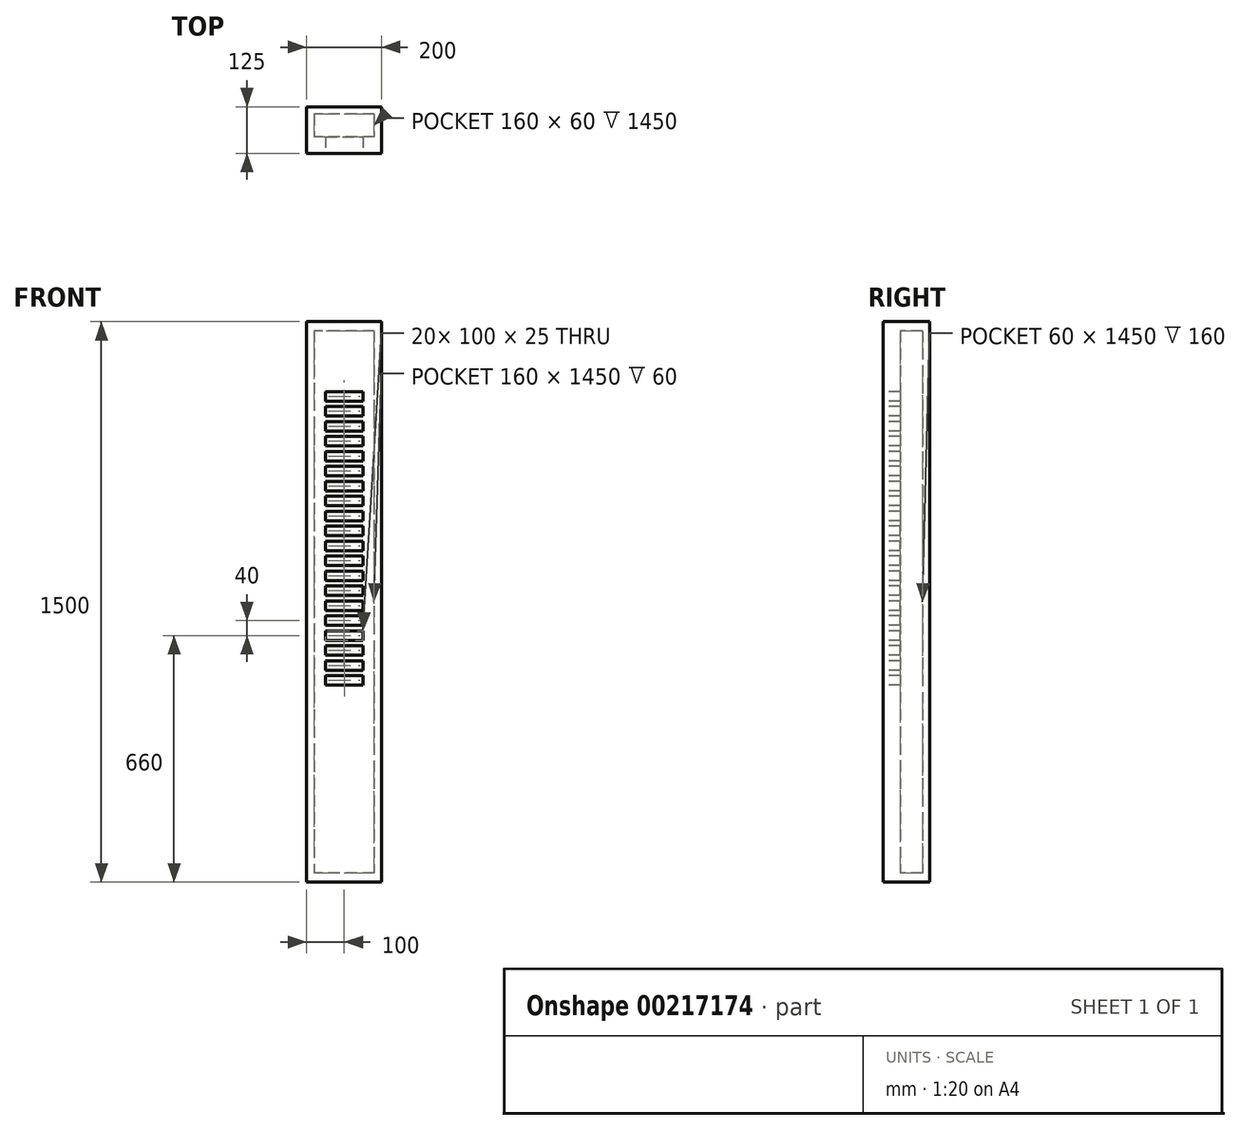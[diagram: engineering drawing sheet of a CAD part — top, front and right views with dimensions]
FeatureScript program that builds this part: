
annotation { "Feature Type Name" : "Feature", "Feature Type Description" : "" }
export const myFeature = defineFeature(function(context is Context, id is Id, definition is map)
    precondition{}
    {
        {
            var Q0;
            Q0=qCreatedBy(makeId("Front.planeOp"),FACE);
            var sketch = newSketch(context, id + "F0", { "sketchPlane" : qUnion([Q0])});
            skLineSegment(sketch, "E0.bottom", {"start": v(-100, 750) * mm, "end": v(100, 750) * mm});
            skLineSegment(sketch, "E0.top", {"start": v(-100, -750) * mm, "end": v(100, -750) * mm});
            skLineSegment(sketch, "E0.left", {"start": v(-100, 750) * mm, "end": v(-100, -750) * mm});
            skLineSegment(sketch, "E0.right", {"start": v(100, 750) * mm, "end": v(100, -750) * mm});
            skLineSegment(sketch, "E1.bottom", {"start": v(-50, 562.5) * mm, "end": v(50, 562.5) * mm});
            skLineSegment(sketch, "E1.top", {"start": v(-50, 537.5) * mm, "end": v(50, 537.5) * mm});
            skLineSegment(sketch, "E1.left", {"start": v(-50, 562.5) * mm, "end": v(-50, 537.5) * mm});
            skLineSegment(sketch, "E1.right", {"start": v(50, 562.5) * mm, "end": v(50, 537.5) * mm});
            skPoint(sketch, "E1.middle", {"position": v(0, 550) * mm});
            skLineSegment(sketch, "E2.bottom", {"start": v(-50, 522.5) * mm, "end": v(50, 522.5) * mm});
            skLineSegment(sketch, "E2.top", {"start": v(-50, 497.5) * mm, "end": v(50, 497.5) * mm});
            skLineSegment(sketch, "E2.left", {"start": v(-50, 522.5) * mm, "end": v(-50, 497.5) * mm});
            skLineSegment(sketch, "E2.right", {"start": v(50, 522.5) * mm, "end": v(50, 497.5) * mm});
            skPoint(sketch, "E2.middle", {"position": v(0, 510) * mm});
            skPoint(sketch, "E2.cornerSnap0", {"position": v(-50, 550) * mm});
            skLineSegment(sketch, "E3.bottom", {"start": v(-50, 482.5) * mm, "end": v(50, 482.5) * mm});
            skLineSegment(sketch, "E3.top", {"start": v(-50, 457.5) * mm, "end": v(50, 457.5) * mm});
            skLineSegment(sketch, "E3.left", {"start": v(-50, 482.5) * mm, "end": v(-50, 457.5) * mm});
            skLineSegment(sketch, "E3.right", {"start": v(50, 482.5) * mm, "end": v(50, 457.5) * mm});
            skPoint(sketch, "E3.middle", {"position": v(0, 470) * mm});
            skLineSegment(sketch, "E4.bottom", {"start": v(-50, 442.5) * mm, "end": v(50, 442.5) * mm});
            skLineSegment(sketch, "E4.top", {"start": v(-50, 417.5) * mm, "end": v(50, 417.5) * mm});
            skLineSegment(sketch, "E4.left", {"start": v(-50, 442.5) * mm, "end": v(-50, 417.5) * mm});
            skLineSegment(sketch, "E4.right", {"start": v(50, 442.5) * mm, "end": v(50, 417.5) * mm});
            skPoint(sketch, "E4.middle", {"position": v(0, 430) * mm});
            skLineSegment(sketch, "E5.bottom", {"start": v(-50, 402.5) * mm, "end": v(50, 402.5) * mm});
            skLineSegment(sketch, "E5.top", {"start": v(-50, 377.5) * mm, "end": v(50, 377.5) * mm});
            skLineSegment(sketch, "E5.left", {"start": v(-50, 402.5) * mm, "end": v(-50, 377.5) * mm});
            skLineSegment(sketch, "E5.right", {"start": v(50, 402.5) * mm, "end": v(50, 377.5) * mm});
            skPoint(sketch, "E5.middle", {"position": v(0, 390) * mm});
            skLineSegment(sketch, "E6.bottom", {"start": v(-50, 362.5) * mm, "end": v(50, 362.5) * mm});
            skLineSegment(sketch, "E6.top", {"start": v(-50, 337.5) * mm, "end": v(50, 337.5) * mm});
            skLineSegment(sketch, "E6.left", {"start": v(-50, 362.5) * mm, "end": v(-50, 337.5) * mm});
            skLineSegment(sketch, "E6.right", {"start": v(50, 362.5) * mm, "end": v(50, 337.5) * mm});
            skPoint(sketch, "E6.middle", {"position": v(0, 350) * mm});
            skLineSegment(sketch, "E7.bottom", {"start": v(-50, 322.5) * mm, "end": v(50, 322.5) * mm});
            skLineSegment(sketch, "E7.top", {"start": v(-50, 297.5) * mm, "end": v(50, 297.5) * mm});
            skLineSegment(sketch, "E7.left", {"start": v(-50, 322.5) * mm, "end": v(-50, 297.5) * mm});
            skLineSegment(sketch, "E7.right", {"start": v(50, 322.5) * mm, "end": v(50, 297.5) * mm});
            skPoint(sketch, "E7.middle", {"position": v(0, 310) * mm});
            skLineSegment(sketch, "E8.bottom", {"start": v(-50, 282.5) * mm, "end": v(50, 282.5) * mm});
            skLineSegment(sketch, "E8.top", {"start": v(-50, 257.5) * mm, "end": v(50, 257.5) * mm});
            skLineSegment(sketch, "E8.left", {"start": v(-50, 282.5) * mm, "end": v(-50, 257.5) * mm});
            skLineSegment(sketch, "E8.right", {"start": v(50, 282.5) * mm, "end": v(50, 257.5) * mm});
            skPoint(sketch, "E8.middle", {"position": v(0, 270) * mm});
            skLineSegment(sketch, "E9.bottom", {"start": v(-50, 242.5) * mm, "end": v(50, 242.5) * mm});
            skLineSegment(sketch, "E9.top", {"start": v(-50, 217.5) * mm, "end": v(50, 217.5) * mm});
            skLineSegment(sketch, "E9.left", {"start": v(-50, 242.5) * mm, "end": v(-50, 217.5) * mm});
            skLineSegment(sketch, "E9.right", {"start": v(50, 242.5) * mm, "end": v(50, 217.5) * mm});
            skPoint(sketch, "E9.middle", {"position": v(0, 230) * mm});
            skPoint(sketch, "E10", {"position": v(0, 210) * mm});
            skLineSegment(sketch, "E11.MirrorCS", {"start": v(-49.95, -142.5) * mm, "end": v(-49.95, -117.5) * mm});
            skLineSegment(sketch, "E12.MirrorCS", {"start": v(50, 17.5) * mm, "end": v(50, 42.5) * mm});
            skLineSegment(sketch, "E13.MirrorCS", {"start": v(-50, 57.5) * mm, "end": v(-50, 82.5) * mm});
            skLineSegment(sketch, "E14.MirrorCS", {"start": v(-50, -62.5) * mm, "end": v(-50, -37.5) * mm});
            skLineSegment(sketch, "E15.MirrorCS", {"start": v(-50, 177.5) * mm, "end": v(-50, 202.5) * mm});
            skLineSegment(sketch, "E16.MirrorCS", {"start": v(-50, 17.5) * mm, "end": v(-50, 42.5) * mm});
            skLineSegment(sketch, "E17.MirrorCS", {"start": v(50, -102.5) * mm, "end": v(50, -77.5) * mm});
            skLineSegment(sketch, "E18.MirrorCS", {"start": v(-50, -102.5) * mm, "end": v(-50, -77.5) * mm});
            skLineSegment(sketch, "E19.MirrorCS", {"start": v(50, -22.5) * mm, "end": v(50, 2.5) * mm});
            skLineSegment(sketch, "E20.MirrorCS", {"start": v(50, 137.5) * mm, "end": v(50, 162.5) * mm});
            skLineSegment(sketch, "E21.MirrorCS", {"start": v(50, -62.5) * mm, "end": v(50, -37.5) * mm});
            skLineSegment(sketch, "E22.MirrorCS", {"start": v(50.05, -142.5) * mm, "end": v(50.05, -117.5) * mm});
            skLineSegment(sketch, "E23.MirrorCS", {"start": v(50, 177.5) * mm, "end": v(50, 202.5) * mm});
            skLineSegment(sketch, "E24.MirrorCS", {"start": v(50, 57.5) * mm, "end": v(50, 82.5) * mm});
            skLineSegment(sketch, "E25.MirrorCS", {"start": v(50, 97.5) * mm, "end": v(50, 122.5) * mm});
            skLineSegment(sketch, "E26.MirrorCS", {"start": v(-50, 97.5) * mm, "end": v(-50, 122.5) * mm});
            skLineSegment(sketch, "E27.MirrorCS", {"start": v(-50, 137.5) * mm, "end": v(-50, 162.5) * mm});
            skLineSegment(sketch, "E28.MirrorCS", {"start": v(-50, -22.5) * mm, "end": v(-50, 2.5) * mm});
            skPoint(sketch, "E29.MirrorP", {"position": v(0, 150) * mm});
            skLineSegment(sketch, "E30.MirrorCS", {"start": v(-50, -77.5) * mm, "end": v(50, -77.5) * mm});
            skLineSegment(sketch, "E31.MirrorCS", {"start": v(-50, 57.5) * mm, "end": v(50, 57.5) * mm});
            skLineSegment(sketch, "E32.MirrorCS", {"start": v(-50, -102.5) * mm, "end": v(50, -102.5) * mm});
            skPoint(sketch, "E33.MirrorP", {"position": v(0, 110) * mm});
            skLineSegment(sketch, "E34.MirrorCS", {"start": v(-50, 97.5) * mm, "end": v(50, 97.5) * mm});
            skPoint(sketch, "E35.MirrorP", {"position": v(0, -50) * mm});
            skLineSegment(sketch, "E36.MirrorCS", {"start": v(-50, 17.5) * mm, "end": v(50, 17.5) * mm});
            skLineSegment(sketch, "E37.MirrorCS", {"start": v(-49.95, -117.5) * mm, "end": v(50.05, -117.5) * mm});
            skPoint(sketch, "E38.MirrorP", {"position": v(0, -90) * mm});
            skLineSegment(sketch, "E39.MirrorCS", {"start": v(-50, 42.5) * mm, "end": v(50, 42.5) * mm});
            skLineSegment(sketch, "E40.MirrorCS", {"start": v(-50, 202.5) * mm, "end": v(50, 202.5) * mm});
            skLineSegment(sketch, "E41.MirrorCS", {"start": v(-50, 2.5) * mm, "end": v(50, 2.5) * mm});
            skPoint(sketch, "E42.MirrorP", {"position": v(0, 30) * mm});
            skLineSegment(sketch, "E43.MirrorCS", {"start": v(-50, 122.5) * mm, "end": v(50, 122.5) * mm});
            skLineSegment(sketch, "E44.MirrorCS", {"start": v(-50, -37.5) * mm, "end": v(50, -37.5) * mm});
            skLineSegment(sketch, "E45.MirrorCS", {"start": v(-50, 177.5) * mm, "end": v(50, 177.5) * mm});
            skLineSegment(sketch, "E46.MirrorCS", {"start": v(-49.95, -142.5) * mm, "end": v(50.05, -142.5) * mm});
            skLineSegment(sketch, "E47.MirrorCS", {"start": v(-50, -62.5) * mm, "end": v(50, -62.5) * mm});
            skPoint(sketch, "E48.MirrorP", {"position": v(0.32, -48.1) * mm});
            skPoint(sketch, "E49.MirrorP", {"position": v(0, 190) * mm});
            skLineSegment(sketch, "E50.MirrorCS", {"start": v(-50, -22.5) * mm, "end": v(50, -22.5) * mm});
            skPoint(sketch, "E51.MirrorP", {"position": v(0, -10) * mm});
            skLineSegment(sketch, "E52.MirrorCS", {"start": v(-50, 137.5) * mm, "end": v(50, 137.5) * mm});
            skPoint(sketch, "E53.MirrorP", {"position": v(0, 70) * mm});
            skLineSegment(sketch, "E54.MirrorCS", {"start": v(-50, 82.5) * mm, "end": v(50, 82.5) * mm});
            skLineSegment(sketch, "E55.MirrorCS", {"start": v(-50, 162.5) * mm, "end": v(50, 162.5) * mm});
            skLineSegment(sketch, "E56.bottom", {"start": v(-49.68, -157.5) * mm, "end": v(50.32, -157.5) * mm});
            skLineSegment(sketch, "E56.top", {"start": v(-49.68, -182.5) * mm, "end": v(50.32, -182.5) * mm});
            skLineSegment(sketch, "E56.left", {"start": v(-49.68, -157.5) * mm, "end": v(-49.68, -182.5) * mm});
            skLineSegment(sketch, "E56.right", {"start": v(50.32, -157.5) * mm, "end": v(50.32, -182.5) * mm});
            skPoint(sketch, "E56.middle", {"position": v(0.32, -170) * mm});
            skLineSegment(sketch, "E57.bottom", {"start": v(-49.68, -197.5) * mm, "end": v(50.32, -197.5) * mm});
            skLineSegment(sketch, "E57.top", {"start": v(-49.68, -222.5) * mm, "end": v(50.32, -222.5) * mm});
            skLineSegment(sketch, "E57.left", {"start": v(-49.68, -197.5) * mm, "end": v(-49.68, -222.5) * mm});
            skLineSegment(sketch, "E57.right", {"start": v(50.32, -197.5) * mm, "end": v(50.32, -222.5) * mm});
            skPoint(sketch, "E57.middle", {"position": v(0.32, -210) * mm});
            skSolve(sketch);
        }
        {
            var Q0;
            Q0 = qSketchRegion(id + "F0", true);
            extrude(context, id + "F1", {"entities" : qUnion([Q0]), "oppositeDirection" : true, "depth" : 20 * mm});
        }
        {
            var Q0;
            Q0=makeQuery(id+"F1.opExtrude","CAP_FACE",FACE,{"disambiguationData":[OSD([sQuery(id+"F0.wireOp",EDGE,"E0.bottom"),sQuery(id+"F0.wireOp",EDGE,"E0.top"),sQuery(id+"F0.wireOp",EDGE,"E0.left"),sQuery(id+"F0.wireOp",EDGE,"E0.right"),sQuery(id+"F0.wireOp",EDGE,"lWsYl7Le-VXsU-LtHt-2v8T-jllIBTfgTiJY.top"),sQuery(id+"F0.wireOp",EDGE,"lWsYl7Le-VXsU-LtHt-2v8T-jllIBTfgTiJY.left"),sQuery(id+"F0.wireOp",EDGE,"lWsYl7Le-VXsU-LtHt-2v8T-jllIBTfgTiJY.right"),sQuery(id+"F0.wireOp",EDGE,"aaVbNj0U-OF5f-4JnV-2Yc2-4G0s3Yt0bnrW"),sQuery(id+"F0.wireOp",EDGE,"OVmzX3q6-0cBj-fLHt-u50l-feVcEXgW18yh.bottom"),sQuery(id+"F0.wireOp",EDGE,"OVmzX3q6-0cBj-fLHt-u50l-feVcEXgW18yh.top"),sQuery(id+"F0.wireOp",EDGE,"OVmzX3q6-0cBj-fLHt-u50l-feVcEXgW18yh.left"),sQuery(id+"F0.wireOp",EDGE,"OVmzX3q6-0cBj-fLHt-u50l-feVcEXgW18yh.right"),sQuery(id+"F0.wireOp",EDGE,"ZMgKGZmY-0Nt6-gGSb-hXb3-GnZd8xFhKWGz.bottom"),sQuery(id+"F0.wireOp",EDGE,"ZMgKGZmY-0Nt6-gGSb-hXb3-GnZd8xFhKWGz.top"),sQuery(id+"F0.wireOp",EDGE,"ZMgKGZmY-0Nt6-gGSb-hXb3-GnZd8xFhKWGz.left"),sQuery(id+"F0.wireOp",EDGE,"ZMgKGZmY-0Nt6-gGSb-hXb3-GnZd8xFhKWGz.right"),sQuery(id+"F0.wireOp",EDGE,"Bwx39Smm-y3T0-mnCU-FLSR-2egvlgzXWiRM.bottom"),sQuery(id+"F0.wireOp",EDGE,"Bwx39Smm-y3T0-mnCU-FLSR-2egvlgzXWiRM.top"),sQuery(id+"F0.wireOp",EDGE,"Bwx39Smm-y3T0-mnCU-FLSR-2egvlgzXWiRM.left"),sQuery(id+"F0.wireOp",EDGE,"Bwx39Smm-y3T0-mnCU-FLSR-2egvlgzXWiRM.right"),sQuery(id+"F0.wireOp",EDGE,"MGwNeILa-x4SI-bGCr-k1i4-DGSqM6lZGJjR.bottom"),sQuery(id+"F0.wireOp",EDGE,"MGwNeILa-x4SI-bGCr-k1i4-DGSqM6lZGJjR.top"),sQuery(id+"F0.wireOp",EDGE,"MGwNeILa-x4SI-bGCr-k1i4-DGSqM6lZGJjR.left"),sQuery(id+"F0.wireOp",EDGE,"MGwNeILa-x4SI-bGCr-k1i4-DGSqM6lZGJjR.right"),sQuery(id+"F0.wireOp",EDGE,"hbvqSmqE-impo-nBCe-z9bM-xYOZ8vVy8rhI.bottom"),sQuery(id+"F0.wireOp",EDGE,"hbvqSmqE-impo-nBCe-z9bM-xYOZ8vVy8rhI.top"),sQuery(id+"F0.wireOp",EDGE,"hbvqSmqE-impo-nBCe-z9bM-xYOZ8vVy8rhI.left"),sQuery(id+"F0.wireOp",EDGE,"hbvqSmqE-impo-nBCe-z9bM-xYOZ8vVy8rhI.right"),sQuery(id+"F0.wireOp",EDGE,"VcGXmmvQ-fiC6-wayE-EPvd-e8lodg97lZlI.bottom"),sQuery(id+"F0.wireOp",EDGE,"VcGXmmvQ-fiC6-wayE-EPvd-e8lodg97lZlI.top"),sQuery(id+"F0.wireOp",EDGE,"VcGXmmvQ-fiC6-wayE-EPvd-e8lodg97lZlI.left"),sQuery(id+"F0.wireOp",EDGE,"VcGXmmvQ-fiC6-wayE-EPvd-e8lodg97lZlI.right"),sQuery(id+"F0.wireOp",EDGE,"Zp1NcbvU-hMgn-Kh3H-kVOq-t8yzjoJBko1y.bottom"),sQuery(id+"F0.wireOp",EDGE,"Zp1NcbvU-hMgn-Kh3H-kVOq-t8yzjoJBko1y.top"),sQuery(id+"F0.wireOp",EDGE,"Zp1NcbvU-hMgn-Kh3H-kVOq-t8yzjoJBko1y.left"),sQuery(id+"F0.wireOp",EDGE,"Zp1NcbvU-hMgn-Kh3H-kVOq-t8yzjoJBko1y.right"),sQuery(id+"F0.wireOp",EDGE,"103cf472-e861-4861-82ab-fd70da238bd10.MirrorCS"),sQuery(id+"F0.wireOp",EDGE,"103cf472-e861-4861-82ab-fd70da238bd11.MirrorCS"),sQuery(id+"F0.wireOp",EDGE,"103cf472-e861-4861-82ab-fd70da238bd12.MirrorCS"),sQuery(id+"F0.wireOp",EDGE,"103cf472-e861-4861-82ab-fd70da238bd13.MirrorCS"),sQuery(id+"F0.wireOp",EDGE,"103cf472-e861-4861-82ab-fd70da238bd14.MirrorCS"),sQuery(id+"F0.wireOp",EDGE,"103cf472-e861-4861-82ab-fd70da238bd15.MirrorCS"),sQuery(id+"F0.wireOp",EDGE,"103cf472-e861-4861-82ab-fd70da238bd16.MirrorCS"),sQuery(id+"F0.wireOp",EDGE,"103cf472-e861-4861-82ab-fd70da238bd17.MirrorCS"),sQuery(id+"F0.wireOp",EDGE,"103cf472-e861-4861-82ab-fd70da238bd18.MirrorCS"),sQuery(id+"F0.wireOp",EDGE,"103cf472-e861-4861-82ab-fd70da238bd19.MirrorCS"),sQuery(id+"F0.wireOp",EDGE,"103cf472-e861-4861-82ab-fd70da238bd110.MirrorCS"),sQuery(id+"F0.wireOp",EDGE,"103cf472-e861-4861-82ab-fd70da238bd111.MirrorCS"),sQuery(id+"F0.wireOp",EDGE,"103cf472-e861-4861-82ab-fd70da238bd112.MirrorCS"),sQuery(id+"F0.wireOp",EDGE,"103cf472-e861-4861-82ab-fd70da238bd113.MirrorCS"),sQuery(id+"F0.wireOp",EDGE,"103cf472-e861-4861-82ab-fd70da238bd114.MirrorCS"),sQuery(id+"F0.wireOp",EDGE,"103cf472-e861-4861-82ab-fd70da238bd115.MirrorCS"),sQuery(id+"F0.wireOp",EDGE,"103cf472-e861-4861-82ab-fd70da238bd116.MirrorCS"),sQuery(id+"F0.wireOp",EDGE,"103cf472-e861-4861-82ab-fd70da238bd117.MirrorCS"),sQuery(id+"F0.wireOp",EDGE,"103cf472-e861-4861-82ab-fd70da238bd118.MirrorCS"),sQuery(id+"F0.wireOp",EDGE,"103cf472-e861-4861-82ab-fd70da238bd119.MirrorCS"),sQuery(id+"F0.wireOp",EDGE,"103cf472-e861-4861-82ab-fd70da238bd120.MirrorCS"),sQuery(id+"F0.wireOp",EDGE,"103cf472-e861-4861-82ab-fd70da238bd121.MirrorCS"),sQuery(id+"F0.wireOp",EDGE,"103cf472-e861-4861-82ab-fd70da238bd122.MirrorCS"),sQuery(id+"F0.wireOp",EDGE,"103cf472-e861-4861-82ab-fd70da238bd123.MirrorCS"),sQuery(id+"F0.wireOp",EDGE,"103cf472-e861-4861-82ab-fd70da238bd124.MirrorCS"),sQuery(id+"F0.wireOp",EDGE,"103cf472-e861-4861-82ab-fd70da238bd125.MirrorCS"),sQuery(id+"F0.wireOp",EDGE,"103cf472-e861-4861-82ab-fd70da238bd126.MirrorCS"),sQuery(id+"F0.wireOp",EDGE,"103cf472-e861-4861-82ab-fd70da238bd127.MirrorCS"),sQuery(id+"F0.wireOp",EDGE,"103cf472-e861-4861-82ab-fd70da238bd128.MirrorCS"),sQuery(id+"F0.wireOp",EDGE,"103cf472-e861-4861-82ab-fd70da238bd130.MirrorCS"),sQuery(id+"F0.wireOp",EDGE,"103cf472-e861-4861-82ab-fd70da238bd131.MirrorCS"),sQuery(id+"F0.wireOp",EDGE,"103cf472-e861-4861-82ab-fd70da238bd132.MirrorCS")])],"isStart":false});
            var sketch = newSketch(context, id + "F2", { "sketchPlane" : qUnion([Q0])});
            skLineSegment(sketch, "E58.bottom", {"start": v(-100, 750) * mm, "end": v(100, 750) * mm});
            skLineSegment(sketch, "E58.top", {"start": v(-100, -750) * mm, "end": v(100, -750) * mm});
            skLineSegment(sketch, "E58.left", {"start": v(-100, 750) * mm, "end": v(-100, -750) * mm});
            skLineSegment(sketch, "E58.right", {"start": v(100, 750) * mm, "end": v(100, -750) * mm});
            skPoint(sketch, "E58.middle", {"position": v(0, 0) * mm});
            skLineSegment(sketch, "E59.bottom", {"start": v(-80, 725) * mm, "end": v(80, 725) * mm});
            skLineSegment(sketch, "E59.top", {"start": v(-80, -725) * mm, "end": v(80, -725) * mm});
            skLineSegment(sketch, "E59.left", {"start": v(-80, 725) * mm, "end": v(-80, -725) * mm});
            skLineSegment(sketch, "E59.right", {"start": v(80, 725) * mm, "end": v(80, -725) * mm});
            skSolve(sketch);
        }
        {
            var Q0;
            Q0=makeQuery(id+"F2.imprint","IMPRINT",FACE,{"disambiguationData":[TD([[makeQuery(id+"F2.imprint","IMPRINT",EDGE,{"derivedFrom":sQuery(id+"F2.wireOp",EDGE,"E58.bottom")}),1.0]])]});
            extrude(context, id + "F3", {"entities" : qUnion([Q0]), "operationType" : NewBodyOperationType.ADD, "depth" : 60 * mm});
        }
        {
            var Q0;
            Q0=makeQuery(id+"F3.opExtrude","CAP_FACE",FACE,{"disambiguationData":[OSD([sQuery(id+"F2.wireOp",EDGE,"E58.bottom"),sQuery(id+"F2.wireOp",EDGE,"E58.top"),sQuery(id+"F2.wireOp",EDGE,"E58.left"),sQuery(id+"F2.wireOp",EDGE,"E58.right"),sQuery(id+"F2.wireOp",EDGE,"E59.bottom"),sQuery(id+"F2.wireOp",EDGE,"E59.top"),sQuery(id+"F2.wireOp",EDGE,"E59.left"),sQuery(id+"F2.wireOp",EDGE,"E59.right")])],"isStart":false});
            var sketch = newSketch(context, id + "F4", { "sketchPlane" : qUnion([Q0])});
            skLineSegment(sketch, "E60.bottom", {"start": v(-100, 750) * mm, "end": v(100, 750) * mm});
            skLineSegment(sketch, "E60.top", {"start": v(-100, -750) * mm, "end": v(100, -750) * mm});
            skLineSegment(sketch, "E60.left", {"start": v(-100, 750) * mm, "end": v(-100, -750) * mm});
            skLineSegment(sketch, "E60.right", {"start": v(100, 750) * mm, "end": v(100, -750) * mm});
            skSolve(sketch);
        }
        {
            var Q0;
            Q0 = qSketchRegion(id + "F4", true);
            extrude(context, id + "F5", {"entities" : qUnion([Q0]), "operationType" : NewBodyOperationType.ADD, "depth" : 20 * mm});
        }
        {
            var Q0;
            Q0=makeQuery(id+"F0.imprint","IMPRINT",FACE,{"disambiguationData":[TD([[makeQuery(id+"F0.imprint","IMPRINT",EDGE,{"derivedFrom":sQuery(id+"F0.wireOp",EDGE,"E0.bottom")}),-1.0]])]});
            extrude(context, id + "F6", {"entities" : qUnion([Q0]), "operationType" : NewBodyOperationType.ADD, "depth" : 25 * mm});
        }
    });
